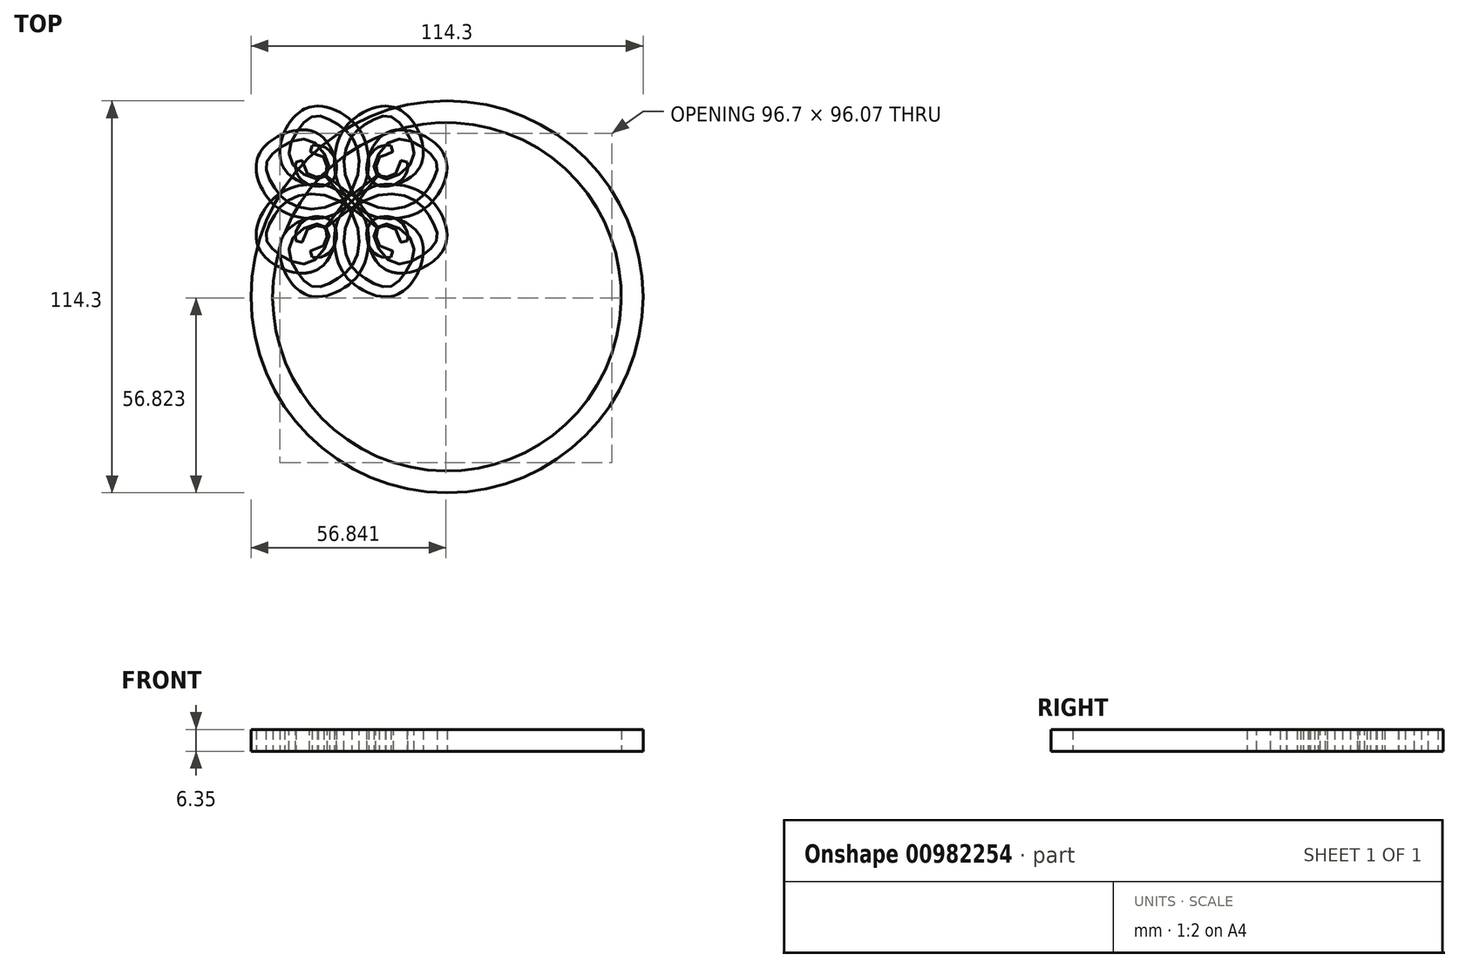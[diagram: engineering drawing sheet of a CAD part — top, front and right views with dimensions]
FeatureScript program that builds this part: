
annotation { "Feature Type Name" : "Feature", "Feature Type Description" : "" }
export const myFeature = defineFeature(function(context is Context, id is Id, definition is map)
    precondition{}
    {
        {
            var Q0;
            Q0=qCreatedBy(makeId("Top.planeOp"),FACE);
            var sketch = newSketch(context, id + "F0", { "sketchPlane" : qUnion([Q0])});
            skArc(sketch, "E0", {"start": v(-48.66, 14.59) * mm, "mid": v(48.04, -16.5) * mm, "end": v(-47.35, 18.4) * mm});
            skLineSegment(sketch, "E1", {"start": v(0, 0) * mm, "end": v(0, 50.8) * mm});
            skLineSegment(sketch, "E2", {"start": v(0, 50.8) * mm, "end": v(0, 0) * mm});
            skLineSegment(sketch, "E3", {"start": v(-50.8, 0) * mm, "end": v(0, 0) * mm});
            skCircle(sketch, "E4.0", {"center": v(0, 0) * mm, "radius": 57.15 * mm});
            skFitSpline(sketch, "E5", {"points": [v(-27.8, 27.8) * mm, v(-22.81, 16.48) * mm, v(-26.12, 6.03) * mm, v(-37.59, 0) * mm, v(-46.04, 5.09) * mm, v(-47.35, 18.4) * mm, v(-34.94, 22.88) * mm, v(-32.48, 16.02) * mm, v(-39.28, 11.58) * mm], "startDerivative": vector(98.02, -98.02) * mm, "endDerivative": vector(-93.18, 22.02) * mm});
            skFitSpline(sketch, "E6", {"points": [v(-35.92, 35.92) * mm, v(-26, 20) * mm, v(-27.52, 9.4) * mm, v(-32.83, 4.7) * mm, v(-38.58, 2.88) * mm, v(-43.74, 7.42) * mm, v(-45.25, 16.52) * mm, v(-35.92, 20.91) * mm, v(-35.92, 14.95) * mm, v(-39.2, 13.79) * mm, v(-39.28, 11.58) * mm], "startDerivative": vector(70.75, -88.56) * mm, "endDerivative": vector(74.44, -44.09) * mm});
            skLineSegment(sketch, "E7.0", {"start": v(-35.01, 36.8) * mm, "end": v(-35.02, 36.82) * mm});
            skLineSegment(sketch, "E8.0", {"start": v(-6.19, 4.4) * mm, "end": v(-12.5, 10.7) * mm});
            skFitSpline(sketch, "E9", {"points": [v(-12.5, 10.7) * mm, v(-11.42, 5.29) * mm, v(-16.47, 0) * mm, v(-21.7, 2.58) * mm, v(-19.98, 9.34) * mm, v(-16.37, 9.98) * mm], "startDerivative": vector(11.96, -27.25) * mm, "endDerivative": vector(29.98, -7.2) * mm});
            skFitSpline(sketch, "E10", {"points": [v(-15.2, 13.4) * mm, v(-13.22, 8.35) * mm, v(-13.85, 4.11) * mm, v(-17.83, 1.68) * mm, v(-20.2, 4.61) * mm, v(-18.92, 7.88) * mm, v(-16.37, 8.65) * mm, v(-16.37, 9.98) * mm], "startDerivative": vector(13.6, -27.9) * mm, "endDerivative": vector(-34.09, 22.74) * mm});
            skFitSpline(sketch, "E11", {"points": [v(-5.78, 0) * mm, v(-7.5, 3.31) * mm, v(-4.32, 4.32) * mm], "startDerivative": vector(-10.51, 6.2) * mm, "endDerivative": vector(13.34, -2.24) * mm});
            skLineSegment(sketch, "E12", {"start": v(-35.92, 35.92) * mm, "end": v(-40.6, 40.22) * mm});
            skLineSegment(sketch, "E13", {"start": v(-50.8, 0) * mm, "end": v(-57.15, 0) * mm});
            skLineSegment(sketch, "E14.trimOffspring", {"start": v(-15.2, 13.4) * mm, "end": v(-23.63, 21.83) * mm});
            skLineSegment(sketch, "E15.trimOffspring", {"start": v(-30.19, 28.4) * mm, "end": v(-36.82, 35.02) * mm});
            skLineSegment(sketch, "E16", {"start": v(0, 0) * mm, "end": v(-35.92, 35.92) * mm});
            skSolve(sketch);
        }
        {
            var Q0;
            {var subQ0=sQuery(id+"F0.wireOp",EDGE,"E6");Q0=makeQuery(id+"F0.imprint","IMPRINT",FACE,{"disambiguationData":[TD([[makeQuery(id+"F0.imprint","IMPRINT",EDGE,{"derivedFrom":subQ0}),1.0]])]});}
            extrude(context, id + "F1", {"entities" : qUnion([Q0]), "depth" : 6.35 * mm, "offsetDistance" : 25.4 * mm});
        }
        {
            var Q0;
            Q0=makeQuery(id+"F1.opExtrude","SWEPT_BODY",BODY,{"disambiguationData":[OSD([sQuery(id+"F0.wireOp",EDGE,"E0"),sQuery(id+"F0.wireOp",EDGE,"E3"),sQuery(id+"F0.wireOp",EDGE,"E4.0"),sQuery(id+"F0.wireOp",EDGE,"E5"),sQuery(id+"F0.wireOp",EDGE,"E6"),sQuery(id+"F0.wireOp",EDGE,"E8.0"),sQuery(id+"F0.wireOp",EDGE,"E9"),sQuery(id+"F0.wireOp",EDGE,"E10"),sQuery(id+"F0.wireOp",EDGE,"E11"),sQuery(id+"F0.wireOp",EDGE,"E12"),sQuery(id+"F0.wireOp",EDGE,"E13"),sQuery(id+"F0.wireOp",EDGE,"E14.trimOffspring"),sQuery(id+"F0.wireOp",EDGE,"E15.trimOffspring"),sQuery(id+"F0.wireOp",EDGE,"E16")])]});
            var Q1;
            Q1=makeQuery(id+"F1.opExtrude","SWEPT_FACE",FACE,{"disambiguationData":[OSD([sQuery(id+"F0.wireOp",EDGE,"E16")])]});
            mirror(context, id + "F2", {"operationType" : NewBodyOperationType.ADD, "entities" : qUnion([Q0]), "mirrorPlane" : qUnion([Q1])});
        }
        {
            var Q0;
            Q0=makeQuery(id+"F1.opExtrude","SWEPT_BODY",BODY,{"disambiguationData":[OSD([sQuery(id+"F0.wireOp",EDGE,"E0"),sQuery(id+"F0.wireOp",EDGE,"E3"),sQuery(id+"F0.wireOp",EDGE,"E4.0"),sQuery(id+"F0.wireOp",EDGE,"E5"),sQuery(id+"F0.wireOp",EDGE,"E6"),sQuery(id+"F0.wireOp",EDGE,"E8.0"),sQuery(id+"F0.wireOp",EDGE,"E9"),sQuery(id+"F0.wireOp",EDGE,"E10"),sQuery(id+"F0.wireOp",EDGE,"E11"),sQuery(id+"F0.wireOp",EDGE,"E12"),sQuery(id+"F0.wireOp",EDGE,"E13"),sQuery(id+"F0.wireOp",EDGE,"E14.trimOffspring"),sQuery(id+"F0.wireOp",EDGE,"E15.trimOffspring"),sQuery(id+"F0.wireOp",EDGE,"E16")])]});
            var Q1;
            {var subQ0=makeQuery(id+"F1.opExtrude","SWEPT_EDGE",EDGE,{"disambiguationData":[OSD([sQuery(id+"F0.wireOp",EDGE,"E2"),sQuery(id+"F0.wireOp",EDGE,"E3"),sQuery(id+"F0.wireOp",EDGE,"E16")])]});Q1=makeQuery(id+"F2.boolean.opBoolean","MERGE",EDGE,{"derivedFrom":[subQ0,makeQuery(id+"F2.opPattern","COPY",EDGE,{"derivedFrom":subQ0,"instanceName":"1"})]});}
            circularPattern(context, id + "F3", {"entities" : qUnion([Q0]), "axis" : qUnion([Q1]), "angle" : 360 * degree, "instanceCount" : 4, "equalSpace" : true});
        }
        {
            var Q0;
            Q0 = qSketchRegion(id + "F0", true);
            extrude(context, id + "F4", {"entities" : qUnion([Q0]), "depth" : 6.35 * mm, "offsetDistance" : 25.4 * mm});
        }
    });
